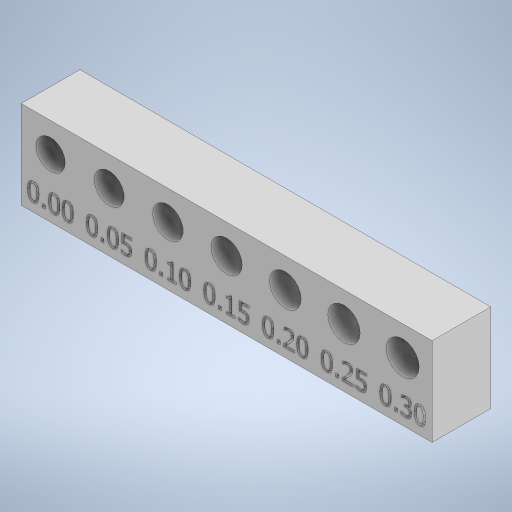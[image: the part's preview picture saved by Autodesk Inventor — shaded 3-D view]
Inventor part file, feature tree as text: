
AUTODESK INVENTOR PART (.ipt)
format: ipt  version: 2023 (Build 270158000, 158)  size: 778,752 bytes
history: native  units: in
note: dims shown in document units (in); Inventor stores cm internally (conversion verified against a paired STEP export)
features: thicken_offset x6, sketch x3, extrude x2, hole x1, pattern_linear x1
ambient origin geometry x8: Origin, YZ Plane, XZ Plane, XY Plane, X Axis, Y Axis, Z Axis, Center Point
bodies: Solid1 (feature_tree)
feature tree (13):
  extrude  "Extrusion1"  Depth=0.3937in
  hole  "Hole1"  [1 undecoded]
  pattern_linear  "Rectangular Pattern1"  Spacing1=0.1969in  [1 undecoded]
  extrude  "Extrusion2"  Depth=0.3937in
  thicken_offset  "Thicken1"
  thicken_offset  "Thicken2"
  thicken_offset  "Thicken3"
  thicken_offset  "Thicken4"
  thicken_offset  "Thicken5"
  thicken_offset  "Thicken6"
  sketch  "Sketch1"  dims[d0=0.3937in d1=0.5906in]
  sketch  "Sketch2"  dims[d2=0.3937in d3=0.0in d4=0.1969in]
  sketch  "Sketch3"  dims[d5=0.1969in d6=0.5in d7=0.1575in d8=0.0787in d9=90.0deg d10=0.315in d11=0.8108in d12=0.1969in d13=2.7559in d15=0.3937in d16=0.3937in d17=0.3937in d18=0.3937in d19=0.3937in d22=0.3937in d23=0.3937in d25=0.1181in d26=0.0197in d27=0.0in d28=0.002in d29=0.002in d30=0.0039in d31=0.0039in d32=0.0059in d33=0.0059in d34=0.0079in d35=0.0079in d36=0.0098in d37=0.0098in d38=0.0118in d39=0.0118in]
note: 2 required parameter values undecoded (feature->parameter linkage not recoverable at this tier; creation-order binding heuristic only, values carry confidence <= 0.55)
